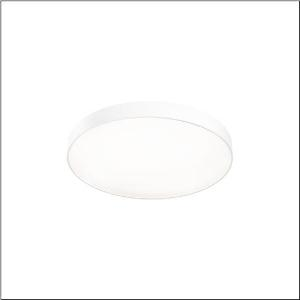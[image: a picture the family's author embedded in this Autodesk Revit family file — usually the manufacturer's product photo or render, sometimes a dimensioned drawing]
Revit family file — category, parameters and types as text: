
# Revit family: round_21_m_51mr36fm8321w
name_source: partatom
category: Lighting Fixtures
units: mm (PartAtom-declared; Revit-internal decimal feet)

## family parameters
Cut with Voids When Loaded = No
Host = Face
Light Source = No
Part Type = Normal
Room Calculation Point = No
Round Connector Dimension = Use Diameter
Shared = No

## types (1)
- --- (1 x LED, 7770 lm, 61.1 W, 3000K)
    Apparent Load = 61 VA
    CIE Flux Codes = 49 80 96 100 100
    Color Rendering = 80
    Color Temperature = 3000K
    Default Elevation = 1800 mm
    Description = Round 21 M, wall and ceiling luminaire, primary optical cover: cover, of PMMA, opal, light emission: direct distribution, primary light characteristic: symmetric, installation type: surface-mounted, suspended mounting, LED, rated luminous flux: 7.700lm, luminous efficacy: 127lm/W, light colour: 830, colour temperature: 3000K, with terminal, 3-pole, mains connection: 230V, AC, 50/60Hz, rated input power: 61W, housing, of aluminium, coated, white, diameter: 600mm, height: 62mm, protection rating (complete): IP40, insulation class (complete): insulation class I (protective earthing), certification: CE, impact resistance: IK04, permissible operating ambient temperature: -10..+35°C, packaging unit: 1 piece
    Height = 87 mm
    Lamp = 1 x LED
    Lamp Light Flux = 7770 lm
    Lamp Power = 61.1 W
    Lamp count = 1
    Length = 600 mm
    Luminous efficacy = 127 lm/W
    Manufacturer = Siteco
    ModVariant = No
    Model = 51MR36FM8321W
    Mounting Place = Ceiling
    Mounting Type = Surface mounted
    Number of Poles = 1
    OnlyDefault = Yes
    Power Factor = 1
    Product Name = Round 21 M
    Product group = wall and ceiling luminaire
    ProductGroupID = 301
    Protection Class = Protection class I
    Protection Degree = IP 40
    RLX_Detail_Level = 1
    RLX_Emergency_Light_Flux = 0 lm
    RLX_Emergency_Type = 0
    RLX_Emergency_Type_DB = No
    RlxData = <blob elided: 14337 chars, md5=d65ccb21>
    Socket = socket
    Standby Power = 0 W
    System Light Flux = 7770 lm
    System Power = 61 W
    Type Comments = factory setting: luminous flux: 100 % | (ON | ON | ON | ON) | 700 mA
    Type Image = l_1258330.jpg
    URL = http://relux.com
    VarID = @adj_009777
    Voltage = 0 V
    Weight = 0.00 kg
    Width = 0 mm  [stored 0 ft]

note: [stored X ft] marks values corroborated as IEEE doubles in the binary element streams (Revit-internal decimal feet)

## geometry (parser evidence)
native form markers: Sweep x13
no freeform markers — native parametric forms only
